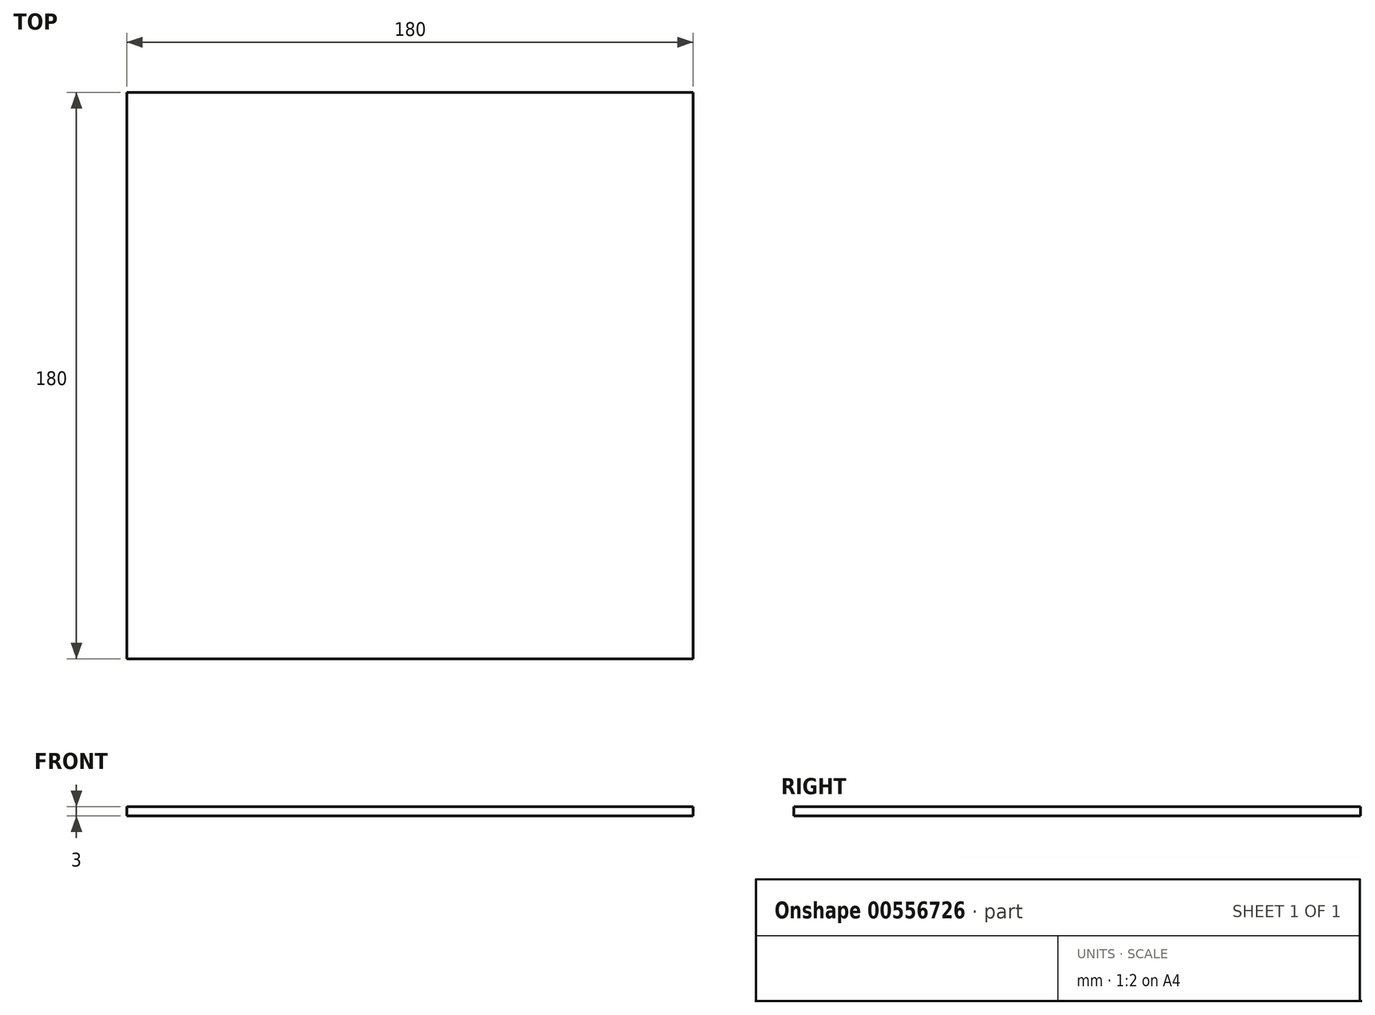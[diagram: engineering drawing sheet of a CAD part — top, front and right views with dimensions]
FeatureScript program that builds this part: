
annotation { "Feature Type Name" : "Feature", "Feature Type Description" : "" }
export const myFeature = defineFeature(function(context is Context, id is Id, definition is map)
    precondition{}
    {
        {
            var Q0;
            Q0=qCreatedBy(makeId("Top.planeOp"),FACE);
            var sketch = newSketch(context, id + "F0", { "sketchPlane" : qUnion([Q0])});
            skLineSegment(sketch, "E0", {"start": v(0, 0) * mm, "end": v(0, 180) * mm});
            skLineSegment(sketch, "E1", {"start": v(0, 180) * mm, "end": v(180, 180) * mm});
            skLineSegment(sketch, "E2", {"start": v(180, 180) * mm, "end": v(180, 0) * mm});
            skLineSegment(sketch, "E3", {"start": v(0, 0) * mm, "end": v(180, 0) * mm});
            skSolve(sketch);
        }
        {
            var Q0;
            Q0=makeQuery(id+"F0.imprint","IMPRINT",FACE,{"disambiguationData":[TD([[makeQuery(id+"F0.imprint","IMPRINT",EDGE,{"derivedFrom":sQuery(id+"F0.wireOp",EDGE,"E0")}),-1.0]])]});
            extrude(context, id + "F1", {"entities" : qUnion([Q0]), "depth" : 3 * mm, "offsetDistance" : 25 * mm});
        }
    });
